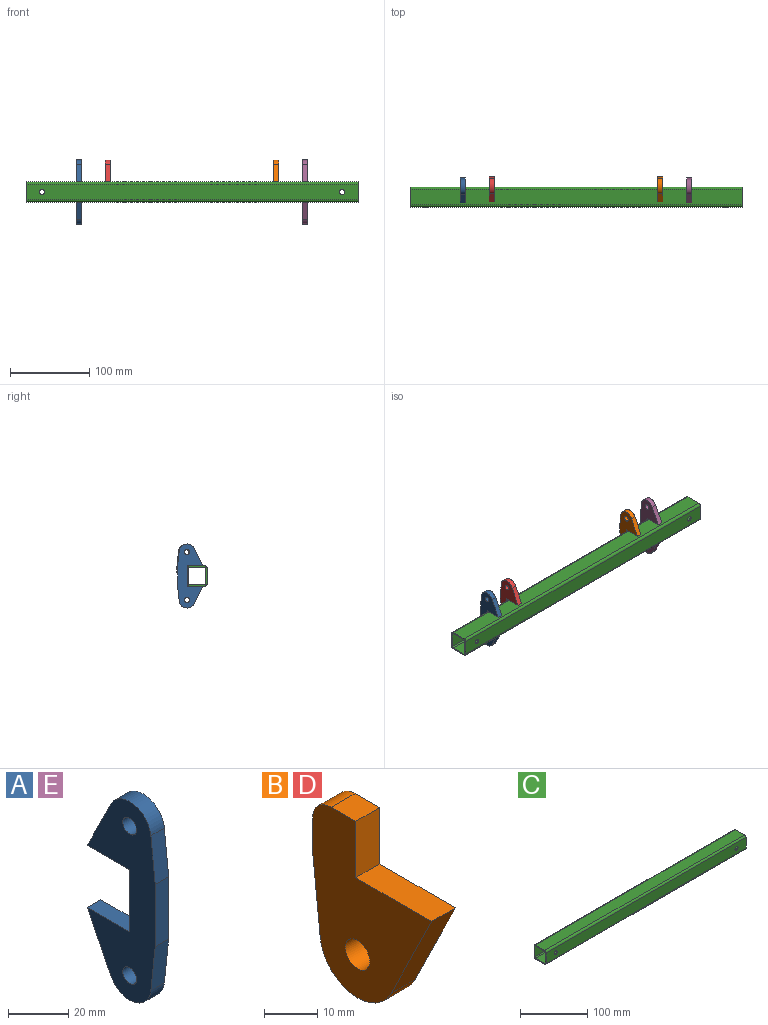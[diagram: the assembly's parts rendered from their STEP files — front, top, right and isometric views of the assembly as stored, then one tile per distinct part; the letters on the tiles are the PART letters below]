
ASSEMBLY  parts=5 mates=4
PART A: 14 faces, bbox 6.4x32x81 mm
  f0: plane 22.25x11.04mm, normal (0,0.9,0.44), area 157.7mm2, adj f1,f10,f12,f13
  f1: cylinder r=10mm len=18.9mm, axis (-1,0,0), area 163.3mm2, adj f0,f2,f12,f13
  f2: plane 18.89x6.35mm, normal (0,-0.99,0.11), area 120.6mm2, adj f1,f3,f12,f13
  f3: plane 25.4x6.35mm, normal (0,-1,0), area 161.3mm2, adj f2,f4,f12,f13
  f4: plane 18.89x6.35mm, normal (0,-0.99,-0.11), area 120.6mm2, adj f3,f5,f12,f13
  f5: cylinder r=10mm len=18.9mm, axis (-1,0,0), area 163.3mm2, adj f4,f6,f12,f13
  f6: plane 22.25x11.04mm, normal (0,0.9,-0.44), area 157.7mm2, adj f5,f7,f12,f13
  f7: plane 20x6.35mm, normal (0,0,1), area 127mm2, adj f6,f8,f12,f13
  f8: plane 25.4x6.35mm, normal (0,1,0), area 161.3mm2, adj f7,f10,f12,f13
  f9: cylinder r=3.25mm len=6.5mm, axis (-1,0,0), area 129.7mm2, adj f12,f13
  f10: plane 20x6.35mm, normal (0,0,-1), area 127mm2, adj f0,f8,f12,f13
  f11: cylinder r=3.25mm len=6.5mm, axis (-1,0,0), area 129.7mm2, adj f12,f13
  f12: plane 81x32mm, normal (1,0,0), area 1503.6mm2, adj f0,f1,f2,f3,f4,f5,f6,f7
  f13: plane 81x32mm, normal (-1,0,0), area 1503.6mm2, adj f0,f1,f2,f3,f4,f5,f6,f7
PART B: 11 faces, bbox 6.4x31.8x40.5 mm
  f0: plane 13x6.35mm, normal (0,-1,0), area 82.6mm2, adj f1,f7,f8,f9
  f1: plane 20.25x6.35mm, normal (0,0,1), area 128.6mm2, adj f0,f2,f8,f9
  f2: plane 21.91x10.78mm, normal (0,-0.9,-0.44), area 155.1mm2, adj f1,f3,f8,f9
  f3: cylinder r=10mm len=18.92mm, axis (-1,0,0), area 163.6mm2, adj f2,f4,f8,f9
  f4: plane 19.07x6.35mm, normal (0,0.99,-0.11), area 121.8mm2, adj f3,f5,f8,f9
  f5: plane 7.5x6.35mm, normal (0,1,0), area 47.6mm2, adj f4,f8,f9,f10
  f6: cylinder r=3.25mm len=6.5mm, axis (-1,0,0), area 129.7mm2, adj f8,f9
  f7: plane 6.5x6.35mm, normal (0,0,1), area 41.3mm2, adj f0,f8,f9,f10
  f8: plane 40.5x31.75mm, normal (1,0,0), area 732.7mm2, adj f0,f1,f2,f3,f4,f5,f6,f7
  f9: plane 40.5x31.75mm, normal (-1,0,0), area 732.7mm2, adj f0,f1,f2,f3,f4,f5,f6,f7
  f10: cylinder r=5mm len=6.35mm, axis (-1,0,0), area 49.9mm2, adj f5,f7,f8,f9
PART C: 22 faces, bbox 420x25.4x25.4 mm
  f0: plane 25.4x25.4mm, normal (1,0,0), area 137.6mm2, adj f1,f2,f3,f4,f6,f7,f8,f9
  f1: plane 420x19.4mm, normal (0,0,-1), area 8148mm2, adj f0,f5,f6,f9
  f2: plane 420x19.4mm, normal (0,1,0), area 8081.6mm2, adj f0,f5,f6,f7,f20,f21
  f3: plane 420x19.4mm, normal (0,0,1), area 8148mm2, adj f0,f5,f7,f8
  f4: plane 420x19.4mm, normal (0,-1,0), area 8081.6mm2, adj f0,f5,f8,f9,f18,f19
  f5: plane 25.4x25.4mm, normal (-1,0,0), area 137.6mm2, adj f1,f2,f3,f4,f6,f7,f8,f9
  f6: cylinder r=3mm len=420mm, axis (-1,0,0), area 1979.2mm2, adj f0,f1,f2,f5
  f7: cylinder r=3mm len=420mm, axis (1,0,0), area 1979.2mm2, adj f0,f2,f3,f5
  f8: cylinder r=3mm len=420mm, axis (-1,0,0), area 1979.2mm2, adj f0,f3,f4,f5
  f9: cylinder r=3mm len=420mm, axis (1,0,0), area 1979.2mm2, adj f0,f1,f4,f5
  f10: plane 420x19.4mm, normal (0,0,1), area 8148mm2, adj f0,f5,f14,f17
  f11: plane 420x19.4mm, normal (0,-1,0), area 8081.6mm2, adj f0,f5,f14,f15,f20,f21
  f12: plane 420x19.4mm, normal (0,0,-1), area 8148mm2, adj f0,f5,f15,f16
  f13: plane 420x19.4mm, normal (0,1,0), area 8081.6mm2, adj f0,f5,f16,f17,f18,f19
  f14: cylinder r=1.5mm len=420mm, axis (-1,0,0), area 989.6mm2, adj f0,f5,f10,f11
  f15: cylinder r=1.5mm len=420mm, axis (1,0,0), area 989.6mm2, adj f0,f5,f11,f12
  f16: cylinder r=1.5mm len=420mm, axis (-1,0,0), area 989.6mm2, adj f0,f5,f12,f13
  f17: cylinder r=1.5mm len=420mm, axis (1,0,0), area 989.6mm2, adj f0,f5,f10,f13
  f18: cylinder r=3.25mm len=6.5mm, axis (0,1,0), area 30.6mm2, adj f4,f13
  f19: cylinder r=3.25mm len=6.5mm, axis (0,1,0), area 30.6mm2, adj f4,f13
  f20: cylinder r=3.25mm len=6.5mm, axis (0,1,0), area 30.6mm2, adj f2,f11
  f21: cylinder r=3.25mm len=6.5mm, axis (0,1,0), area 30.6mm2, adj f2,f11
PART D: same geometry as B
PART E: same geometry as A
PLACE A rot(axis=(0,0,1),180deg) t=(76.08,316.91,-65.52)mm
PLACE B rot(axis=(0,1,0),180deg) t=(235.18,5.41,33.98)mm
PLACE C t=(76.08,-183.09,-65.52)mm fixed
PLACE D rot(axis=(0,1,0),180deg) t=(21.53,5.41,33.98)mm
PLACE E rot(axis=(0,0,1),180deg) t=(362.44,316.91,-65.52)mm
MATE fastened A.f8 <-> C.f2  axis (0,-1,0) through (-70.27,79.61,34.48)mm
MATE fastened B.f1 <-> C.f3  axis (0,0,-1) through (186.08,70.79,47.18)mm
MATE fastened D.f1 <-> C.f3  axis (0,0,-1) through (-33.92,70.79,47.18)mm
MATE fastened C.f2 <-> E.f8  axis (0,1,0) through (286.08,79.61,34.48)mm
